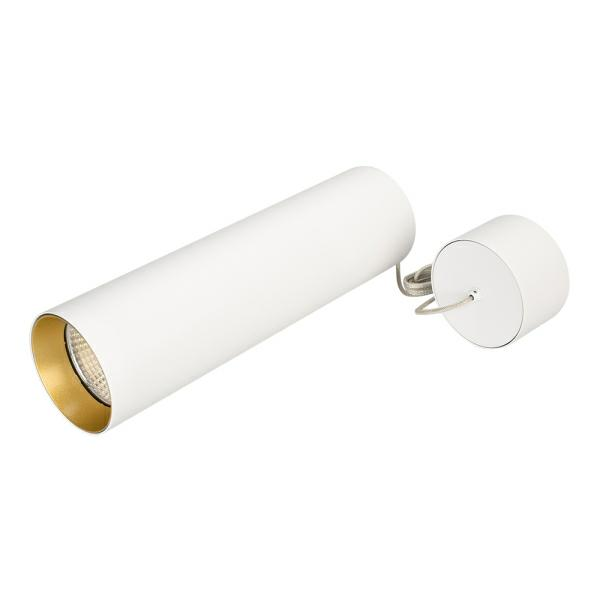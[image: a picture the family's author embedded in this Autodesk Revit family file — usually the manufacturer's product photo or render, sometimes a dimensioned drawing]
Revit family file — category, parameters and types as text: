
# Revit family: POLO-HANG-LONG300
name_source: partatom
category: Осветительные приборы
revit_build: Autodesk Revit 2017 (Build: 20160225_1515(x64)
units: mm (PartAtom-declared; Revit-internal decimal feet)

## family parameters
Всегда вертикально = Да
Источник света = Да
На основе рабочей плоскости = Нет
Общий = Нет
При загрузке вырезать с полостями = Нет
Размер круглого соединителя = Использовать диаметр
Тип детали = Нормальный
Точка расчета площади = Нет

## types (18) — shared parameters
ADSK_Единица измерения = шт.
ADSK_Завод-изготовитель = ARLIGHT
ADSK_Классификация нагрузок = Освещение
ADSK_Количество фаз = 1
ADSK_Количество фаз числовое = 1
ADSK_Коэффициент мощности = 0.9
ADSK_Масса_Текст = 1.26
ADSK_Наименование = Светильник
ADSK_Напряжение = 230 В
ADSK_Номинальная мощность = 15 Вт
ADSK_Полная мощность = 17 В·А
ADSK_Размер_Диаметр = 85 мм
ADSK_Размер_Длина = 300 мм
ADSK_Ток = 0 А
ARL_Драйвер = Встроенный (PRI:220-240VAC)
ARL_Индекс цветопередачи = >80
ARL_Класс защиты от поражения электрическим током = I
ARL_Класс пылевлагозащиты = IP20
ARL_Область использования = Категория размещения - 4
ARL_Рабочая температура окружающей среды = -25…+45
ARL_Серия = POLO
ARL_Способ монтажа = Подвесной
ARL_Тип товара = Светильник
ARL_Угол обзора = 40°
URL = https://arlight.ru
Видимая форма излучения при визуализации = Нет
Группа модели = Светильники
Изготовитель = ARLIGHT
Изготовитель (сайт) = www.arlight.ru
Изготовитель (телефон) = 8 800 505 26 29
Излучение по диаметру окружности = 81 мм
Полная установленная мощность = 17 В·А
Разработчик = НТЦ Конструктор
Разработчик (URL) = https://constructor.ru
Разработчик (телефон) = +7 (495) 781-05-35
Светофильтр = 16777215
Смещение цветовой температуры при затухании лампы = <Нет>
Угол наклона = 90.00°

## per-type parameters (varying)
| type | ADSK_Код изделия | ADSK_Марка | ARL_Материал вставки | ARL_Материал корпуса | ARL_Обозначение корпуса | ARL_Цвет покрытия | ARL_Цвет свечения | Комментарии к типоразмеру | Описание | Файл фотометрической сетки |
| 027419 Светильник SP-POLO-HANG-LONG300-R85-15W White5000 (WH-BK, 40 deg) | Арт. 027419 | SP-POLO-HANG-LONG300-R85-15W White5000 | Металл, чёрный | Металл, белый | Корпус круглый, металл, цвет белый | Белый | Дневной 5000K | Арт. 027419 | Подвесной светильник 15 Вт, белый круглый корпус, черная вставка, металл. Цвет свечения БЕЛЫЙ 5000K, св.поток 1100лм, CRI(Ra)>80, угол 40°. Размер Ø85x300 мм, встроенный драйвер PRI:220-240VAC, SEC:DC 350mA 30-43V 15 Вт | 027419 SP-POLO-HANG-LONG300-R85-15W White5000 (WH-BK, 40 deg).ies |
| 027421 Светильник SP-POLO-HANG-LONG300-R85-15W White5000 (WH-GD, 40 deg) | Арт. 027421 | SP-POLO-HANG-LONG300-R85-15W White5000 | Металл, цветной | Металл, белый | Корпус круглый, металл, цвет белый | Белый | Дневной 5000K | Арт. 027421 | Подвесной светильник 15 Вт, белый круглый корпус, цветная вставка, металл. Цвет свечения БЕЛЫЙ 5000K, св.поток 1100лм, CRI(Ra)>80, угол 40°. Размер Ø85x300 мм, встроенный драйвер PRI:220-240VAC, SEC:DC 350mA 30-43V 15 Вт | 027421 SP-POLO-HANG-LONG300-R85-15W White5000 (WH-GD, 40 deg).ies |
| 027420 Светильник SP-POLO-HANG-LONG300-R85-15W White5000 (WH-WH, 40 deg) | Арт. 027420 | SP-POLO-HANG-LONG300-R85-15W White5000 | Металл, белый | Металл, белый | Корпус круглый, металл, цвет белый | Белый | Дневной 5000K | Арт. 027420 | Подвесной светильник 15 Вт, белый круглый корпус, белая вставка, металл. Цвет свечения БЕЛЫЙ 5000K, св.поток 1100лм, CRI(Ra)>80, угол 40°. Размер Ø85x300 мм, встроенный драйвер PRI:220-240VAC, SEC:DC 350mA 30-43V 15 Вт | 027420 SP-POLO-HANG-LONG300-R85-15W White5000 (WH-WH, 40 deg).ies |
| 027407 Светильник SP-POLO-HANG-LONG300-R85-15W Day4000 (WH-BK, 40 deg) | Арт. 027407 | SP-POLO-HANG-LONG300-R85-15W Day4000 | Металл, чёрный | Металл, белый | Корпус круглый, металл, цвет белый | Белый | Дневной 4000K | Арт. 027407 | Подвесной светильник 15 Вт, белый круглый корпус, черная вставка, металл. Цвет свечения ДНЕВНОЙ 4000K, св.поток 1100лм, CRI(Ra)>80, угол 40°. Размер Ø85x300 мм, встроенный драйвер PRI:220-240VAC, SEC:DC 350mA 30-43V 15 Вт | 027407 SP-POLO-HANG-LONG300-R85-15W Day4000 (WH-BK, 40 deg).ies |
| 027409 Светильник SP-POLO-HANG-LONG300-R85-15W Day4000 (WH-GD, 40 deg) | Арт. 027409 | SP-POLO-HANG-LONG300-R85-15W Day4000 | Металл, цветной | Металл, белый | Корпус круглый, металл, цвет белый | Белый | Дневной 4000K | Арт. 027409 | Подвесной светильник 15 Вт, белый круглый корпус, цветная вставка, металл. Цвет свечения ДНЕВНОЙ 4000K, св.поток 1100лм, CRI(Ra)>80, угол 40°. Размер Ø85x300 мм, встроенный драйвер PRI:220-240VAC, SEC:DC 350mA 30-43V 15 Вт | 027409 SP-POLO-HANG-LONG300-R85-15W Day4000 (WH-GD, 40 deg).ies |
| 027408 Светильник SP-POLO-HANG-LONG300-R85-15W Day4000 (WH-WH, 40 deg) | Арт. 027408 | SP-POLO-HANG-LONG300-R85-15W Day4000 | Металл, белый | Металл, белый | Корпус круглый, металл, цвет белый | Белый | Дневной 4000K | Арт. 027408 | Подвесной светильник 15 Вт, белый круглый корпус, белая вставка, металл. Цвет свечения ДНЕВНОЙ 4000K, св.поток 1100лм, CRI(Ra)>80, угол 40°. Размер Ø85x300 мм, встроенный драйвер PRI:220-240VAC, SEC:DC 350mA 30-43V 15 Вт | 027408 SP-POLO-HANG-LONG300-R85-15W Day4000 (WH-WH, 40 deg).ies |
| 027413 Светильник SP-POLO-HANG-LONG300-R85-15W Warm3000 (WH-BK, 40 deg) | Арт. 027413 | SP-POLO-HANG-LONG300-R85-15W Warm3000 | Металл, чёрный | Металл, белый | Корпус круглый, металл, цвет белый | Белый | Теплый 3000K | Арт. 027413 | Подвесной светильник 15 Вт, белый круглый корпус, черная вставка, металл. Цвет свечения БЕЛЫЙ ТЕПЛЫЙ 3000K, св.поток 1100лм, CRI(Ra)>80, угол 40°. Размер Ø85x300 мм, встроенный драйвер PRI:220-240VAC, SEC:DC 350mA 30-43V 15 Вт | 027413 SP-POLO-HANG-LONG300-R85-15W Warm3000 (WH-BK, 40 deg).ies |
| 027415 Светильник SP-POLO-HANG-LONG300-R85-15W Warm3000 (WH-GD, 40 deg) | Арт. 027415 | SP-POLO-HANG-LONG300-R85-15W Warm3000 | Металл, цветной | Металл, белый | Корпус круглый, металл, цвет белый | Белый | Теплый 3000K | Арт. 027415 | Подвесной светильник 15 Вт, белый круглый корпус, цветная вставка, металл. Цвет свечения БЕЛЫЙ ТЕПЛЫЙ 3000K, св.поток 1100лм, CRI(Ra)>80, угол 40°. Размер Ø85x300 мм, встроенный драйвер PRI:220-240VAC, SEC:DC 350mA 30-43V 15 Вт | 027415 SP-POLO-HANG-LONG300-R85-15W Warm3000 (WH-GD, 40 deg).ies |
| 027414 Светильник SP-POLO-HANG-LONG300-R85-15W Warm3000 (WH-WH, 40 deg) | Арт. 027414 | SP-POLO-HANG-LONG300-R85-15W Warm3000 | Металл, белый | Металл, белый | Корпус круглый, металл, цвет белый | Белый | Теплый 3000K | Арт. 027414 | Подвесной светильник 15 Вт, белый круглый корпус, белая вставка, металл. Цвет свечения БЕЛЫЙ ТЕПЛЫЙ 3000K, св.поток 1100лм, CRI(Ra)>80, угол 40°. Размер Ø85x300 мм, встроенный драйвер PRI:220-240VAC, SEC:DC 350mA 30-43V 15 Вт | 027414 SP-POLO-HANG-LONG300-R85-15W Warm3000 (WH-WH, 40 deg).ies |
| 027416 Светильник SP-POLO-HANG-LONG300-R85-15W White5000 (BK-BK, 40 deg) | Арт. 027416 | SP-POLO-HANG-LONG300-R85-15W White5000 | Металл, чёрный | Металл, чёрный | Корпус круглый, металл, цвет черный | Черный | Дневной 5000K | Арт. 027416 | Подвесной светильник 15 Вт, черный круглый корпус, черная вставка, металл. Цвет свечения БЕЛЫЙ 5000K, св.поток 1100лм, CRI(Ra)>80, угол 40°. Размер Ø85x300 мм, встроенный драйвер PRI:220-240VAC, SEC:DC 350mA 30-43V 15 Вт | 027416 SP-POLO-HANG-LONG300-R85-15W White5000 (BK-BK, 40 deg).ies |
| 027418 Светильник SP-POLO-HANG-LONG300-R85-15W White5000 (BK-GD, 40 deg) | Арт. 027418 | SP-POLO-HANG-LONG300-R85-15W White5000 | Металл, цветной | Металл, чёрный | Корпус круглый, металл, цвет черный | Черный | Дневной 5000K | Арт. 027418 | Подвесной светильник 15 Вт, черный круглый корпус, цветная вставка, металл. Цвет свечения БЕЛЫЙ 5000K, св.поток 1100лм, CRI(Ra)>80, угол 40°. Размер Ø85x300 мм, встроенный драйвер PRI:220-240VAC, SEC:DC 350mA 30-43V 15 Вт | 027418 SP-POLO-HANG-LONG300-R85-15W White5000 (BK-GD, 40 deg).ies |
| 027417 Светильник SP-POLO-HANG-LONG300-R85-15W White5000 (BK-WH, 40 deg) | Арт. 027417 | SP-POLO-HANG-LONG300-R85-15W White5000 | Металл, белый | Металл, чёрный | Корпус круглый, металл, цвет черный | Черный | Дневной 5000K | Арт. 027417 | Подвесной светильник 15 Вт, черный круглый корпус, белая вставка, металл. Цвет свечения БЕЛЫЙ 5000K, св.поток 1100лм, CRI(Ra)>80, угол 40°. Размер Ø85x300 мм, встроенный драйвер PRI:220-240VAC, SEC:DC 350mA 30-43V 15 Вт | 027417 SP-POLO-HANG-LONG300-R85-15W White5000 (BK-WH, 40 deg).ies |
| 027372 Светильник SP-POLO-HANG-LONG300-R85-15W Day4000 (BK-BK, 40 deg) | Арт. 027372 | SP-POLO-HANG-LONG300-R85-15W Day4000 | Металл, чёрный | Металл, чёрный | Корпус круглый, металл, цвет черный | Черный | Дневной 4000K | Арт. 027372 | Подвесной светильник 15 Вт, черный круглый корпус, черная вставка, металл. Цвет свечения ДНЕВНОЙ 4000K, св.поток 1100лм, CRI(Ra)>80, угол 40°. Размер Ø85x300 мм, встроенный драйвер PRI:220-240VAC, SEC:DC 350mA 30-43V 15 Вт | 027372 SP-POLO-HANG-LONG300-R85-15W Day4000 (BK-BK, 40 deg).ies |
| 027406 Светильник SP-POLO-HANG-LONG300-R85-15W Day4000 (BK-GD, 40 deg) | Арт. 027406 | SP-POLO-HANG-LONG300-R85-15W Day4000 | Металл, цветной | Металл, чёрный | Корпус круглый, металл, цвет черный | Черный | Дневной 4000K | Арт. 027406 | Подвесной светильник 15 Вт, черный круглый корпус, цветная вставка, металл. Цвет свечения ДНЕВНОЙ 4000K, св.поток 1100лм, CRI(Ra)>80, угол 40°. Размер Ø85x300 мм, встроенный драйвер PRI:220-240VAC, SEC:DC 350mA 30-43V 15 Вт | 027406 SP-POLO-HANG-LONG300-R85-15W Day4000 (BK-GD, 40 deg).ies |
| 027405 Светильник SP-POLO-HANG-LONG300-R85-15W Day4000 (BK-WH, 40 deg) | Арт. 027405 | SP-POLO-HANG-LONG300-R85-15W Day4000 | Металл, белый | Металл, чёрный | Корпус круглый, металл, цвет черный | Черный | Дневной 4000K | Арт. 027405 | Подвесной светильник 15 Вт, черный круглый корпус, белая вставка, металл. Цвет свечения ДНЕВНОЙ 4000K, св.поток 1100лм, CRI(Ra)>80, угол 40°. Размер Ø85x300 мм, встроенный драйвер PRI:220-240VAC, SEC:DC 350mA 30-43V 15 Вт | 027405 SP-POLO-HANG-LONG300-R85-15W Day4000 (BK-WH, 40 deg).ies |
| 027410 Светильник SP-POLO-HANG-LONG300-R85-15W Warm3000 (BK-BK, 40 deg) | Арт. 027410 | SP-POLO-HANG-LONG300-R85-15W Warm3000 | Металл, чёрный | Металл, чёрный | Корпус круглый, металл, цвет черный | Черный | Теплый 3000K | Арт. 027410 | Подвесной светильник 15 Вт, черный круглый корпус, черная вставка, металл. Цвет свечения БЕЛЫЙ ТЕПЛЫЙ 3000K, св.поток 1100лм, CRI(Ra)>80, угол 40°. Размер Ø85x300 мм, встроенный драйвер PRI:220-240VAC, SEC:DC 350mA 30-43V 15 Вт | 027410 SP-POLO-HANG-LONG300-R85-15W Warm3000 (BK-BK, 40 deg).ies |
| 027412 Светильник SP-POLO-HANG-LONG300-R85-15W Warm3000 (BK-GD, 40 deg) | Арт. 027412 | SP-POLO-HANG-LONG300-R85-15W Warm3000 | Металл, цветной | Металл, чёрный | Корпус круглый, металл, цвет черный | Черный | Теплый 3000K | Арт. 027412 | Подвесной светильник 15 Вт, черный круглый корпус, цветная вставка, металл. Цвет свечения БЕЛЫЙ ТЕПЛЫЙ 3000K, св.поток 1100лм, CRI(Ra)>80, угол 40°. Размер Ø85x300 мм, встроенный драйвер PRI:220-240VAC, SEC:DC 350mA 30-43V 15 Вт | 027412 SP-POLO-HANG-LONG300-R85-15W Warm3000 (BK-GD, 40 deg).ies |
| 027411 Светильник SP-POLO-HANG-LONG300-R85-15W Warm3000 (BK-WH, 40 deg) | Арт. 027411 | SP-POLO-HANG-LONG300-R85-15W Warm3000 | Металл, белый | Металл, чёрный | Корпус круглый, металл, цвет черный | Черный | Теплый 3000K | Арт. 027411 | Подвесной светильник 15 Вт, черный круглый корпус, белая вставка, металл. Цвет свечения БЕЛЫЙ ТЕПЛЫЙ 3000K, св.поток 1100лм, CRI(Ra)>80, угол 40°. Размер Ø85x300 мм, встроенный драйвер PRI:220-240VAC, SEC:DC 350mA 30-43V 15 Вт | 027411 SP-POLO-HANG-LONG300-R85-15W Warm3000 (BK-WH, 40 deg).ies |
